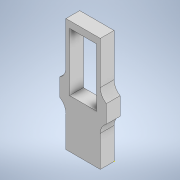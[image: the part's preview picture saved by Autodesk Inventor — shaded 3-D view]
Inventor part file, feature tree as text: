
AUTODESK INVENTOR PART (.ipt)
format: ipt  version: 2021.2 (Build 252289000, 289)  size: 157,184 bytes
history: native  units: in
note: dims shown in document units (in); Inventor stores cm internally (conversion verified against a paired STEP export)
features: sketch x6, extrude x5, fillet x2
ambient origin geometry x8: Origin, YZ Plane, XZ Plane, XY Plane, X Axis, Y Axis, Z Axis, Center Point
bodies: Solid1 (feature_tree)
feature tree (13):
  extrude  "Extrusion1"  Depth=3.0in
  sketch  "Sketch2"  dims[d14=0.3937in d15=0.3937in]
  extrude  "Extrusion2"  Depth=0.3937in
  extrude  "Extrusion3"  Depth=0.7874in
  extrude  "Extrusion4"  Depth=0.4in TaperAngle=0.0deg
  fillet  "Fillet1"  Radius=0.8in
  extrude  "Extrusion5"  Depth=0.375in
  fillet  "Fillet2"  Radius=0.175in
  sketch  "Sketch1"  dims[d0=1.0in d1=3.0in]
  sketch  "Sketch3"  dims[d16=0.7874in d17=1.5866in]
  sketch  "Sketch4"  dims[d18=0.4in d19=0.0in d20=0.3in d21=0.0in d22=0.8in d23=0.0in]
  sketch  "Sketch5"  dims[d24=0.175in d25=0.0in d26=0.375in d27=0.175in d28=0.0in]
  sketch  "Sketch6"  dims[d29=0.375in]
